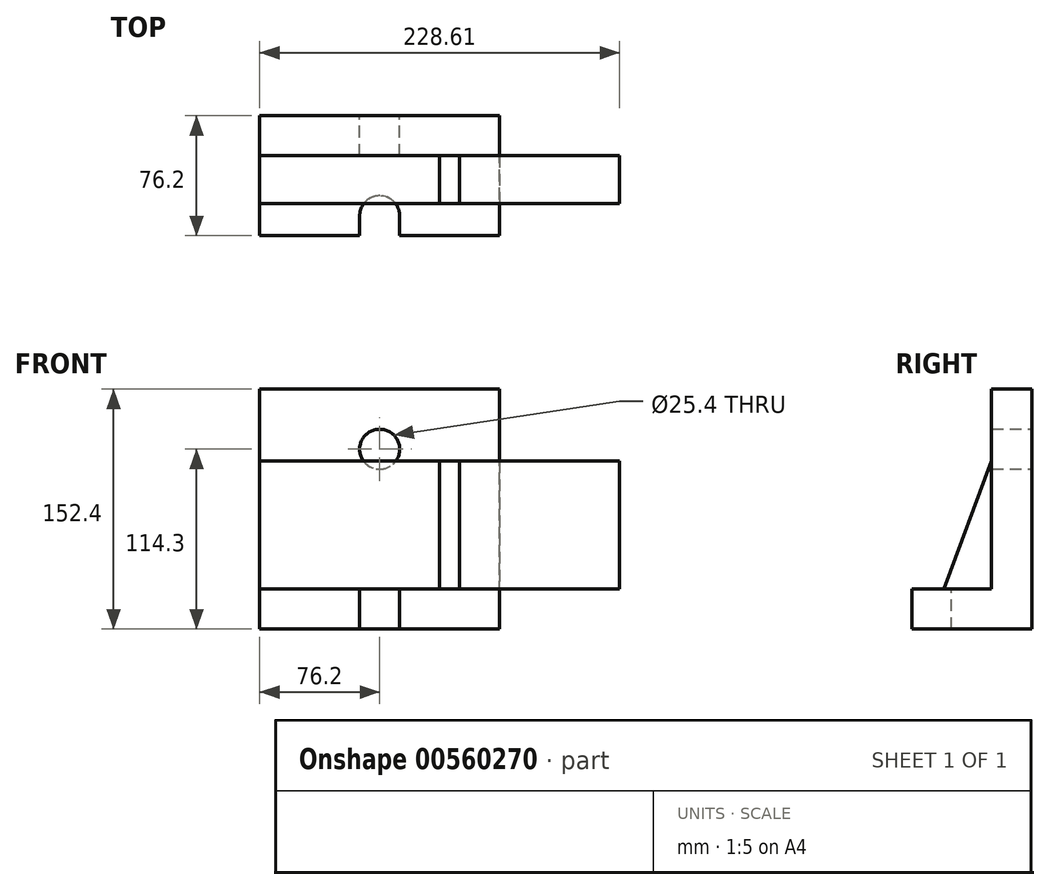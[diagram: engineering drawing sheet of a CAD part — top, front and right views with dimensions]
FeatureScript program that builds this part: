
annotation { "Feature Type Name" : "Feature", "Feature Type Description" : "" }
export const myFeature = defineFeature(function(context is Context, id is Id, definition is map)
    precondition{}
    {
        {
            var Q0;
            Q0=qCreatedBy(makeId("Right.planeOp"),FACE);
            var sketch = newSketch(context, id + "F0", { "sketchPlane" : qUnion([Q0])});
            skLineSegment(sketch, "E0", {"start": v(0, 0) * mm, "end": v(0, 152.4) * mm});
            skLineSegment(sketch, "E1", {"start": v(0, 152.4) * mm, "end": v(-25.4, 152.4) * mm});
            skLineSegment(sketch, "E2", {"start": v(-25.4, 152.4) * mm, "end": v(-25.4, 25.4) * mm});
            skLineSegment(sketch, "E3", {"start": v(-25.4, 25.4) * mm, "end": v(-76.2, 25.4) * mm});
            skLineSegment(sketch, "E4", {"start": v(-76.2, 25.4) * mm, "end": v(-76.2, 0) * mm});
            skLineSegment(sketch, "E5", {"start": v(-76.2, 0) * mm, "end": v(0, 0) * mm});
            skSolve(sketch);
        }
        {
            var Q0;
            Q0=makeQuery(id+"F0.imprint","IMPRINT",FACE,{"disambiguationData":[TD([[makeQuery(id+"F0.imprint","IMPRINT",EDGE,{"derivedFrom":sQuery(id+"F0.wireOp",EDGE,"E0")}),1.0]])]});
            extrude(context, id + "F1", {"entities" : qUnion([Q0]), "endBound" : BoundingType.SYMMETRIC, "depth" : 152.4 * mm, "offsetDistance" : 25.4 * mm});
        }
        {
            var Q0;
            Q0=makeQuery(id+"F1.opExtrude","SWEPT_FACE",FACE,{"disambiguationData":[OSD([sQuery(id+"F0.wireOp",EDGE,"E0")])]});
            var sketch = newSketch(context, id + "F2", { "sketchPlane" : qUnion([Q0])});
            skCircle(sketch, "E6", {"center": v(0, 114.3) * mm, "radius": 12.7 * mm});
            skPoint(sketch, "E6.centerSnap0", {"position": v(0, 152.4) * mm});
            skSolve(sketch);
        }
        {
            var Q0;
            Q0=makeQuery(id+"F2.imprint","IMPRINT",FACE,{"disambiguationData":[TD([[makeQuery(id+"F2.imprint","IMPRINT",EDGE,{"derivedFrom":sQuery(id+"F2.wireOp",EDGE,"E6")}),1.0]])]});
            extrude(context, id + "F3", {"entities" : qUnion([Q0]), "operationType" : NewBodyOperationType.REMOVE, "endBound" : BoundingType.THROUGH_ALL, "oppositeDirection" : true, "depth" : 25.4 * mm, "offsetDistance" : 25.4 * mm});
        }
        {
            var Q0;
            Q0=makeQuery(id+"F1.opExtrude","SWEPT_FACE",FACE,{"disambiguationData":[OSD([sQuery(id+"F0.wireOp",EDGE,"E3")])]});
            var sketch = newSketch(context, id + "F4", { "sketchPlane" : qUnion([Q0])});
            skCircle(sketch, "E7", {"center": v(0, -63.5) * mm, "radius": 12.7 * mm});
            skPoint(sketch, "E7.centerSnap0", {"position": v(0, -76.2) * mm});
            skLineSegment(sketch, "E8", {"start": v(-12.7, -63.5) * mm, "end": v(-12.7, -76.2) * mm});
            skLineSegment(sketch, "E9", {"start": v(12.7, -63.5) * mm, "end": v(12.7, -76.2) * mm});
            skSolve(sketch);
        }
        {
            var Q0;
            {var subQ0=sQuery(id+"F4.wireOp",EDGE,"E7");var subQ1=makeQuery(id+"F4.imprint","INTERSECT",VERTEX,{"derivedFrom":[subQ0,sQuery(id+"F4.wireOp",EDGE,"E8")]});Q0=makeQuery(id+"F4.imprint","IMPRINT",FACE,{"disambiguationData":[TD([[makeQuery(id+"F4.imprint","IMPRINT",EDGE,{"disambiguationData":[TD([[subQ1,1.0]])],"derivedFrom":subQ0}),1.0]])]});}
            var Q1;
            {var subQ0=sQuery(id+"F4.wireOp",EDGE,"E8");Q1=makeQuery(id+"F4.imprint","IMPRINT",FACE,{"disambiguationData":[TD([[makeQuery(id+"F4.imprint","IMPRINT",EDGE,{"derivedFrom":subQ0}),1.0]])]});}
            var Q2;
            {var subQ0=sQuery(id+"F4.wireOp",EDGE,"E9");Q2=makeQuery(id+"F4.imprint","IMPRINT",FACE,{"disambiguationData":[TD([[makeQuery(id+"F4.imprint","IMPRINT",EDGE,{"derivedFrom":subQ0}),-1.0]])]});}
            extrude(context, id + "F5", {"entities" : qUnion([Q0, Q1, Q2]), "operationType" : NewBodyOperationType.REMOVE, "endBound" : BoundingType.THROUGH_ALL, "oppositeDirection" : true, "depth" : 25.4 * mm, "offsetDistance" : 25.4 * mm});
        }
        {
            var Q0;
            Q0=qCreatedBy(makeId("Right.planeOp"),FACE);
            cPlane(context, id + "F6", {"entities" : qUnion([Q0]), "cplaneType" : CPlaneType.OFFSET, "offset" : 50.8 * mm, "width" : 152.4 * mm, "height" : 152.4 * mm});
        }
        {
            var Q0;
            Q0=qCreatedBy(id+"F6.planeOp",FACE);
            var sketch = newSketch(context, id + "F7", { "sketchPlane" : qUnion([Q0])});
            skLineSegment(sketch, "E10.0", {"start": v(-25.4, 106.68) * mm, "end": v(-25.4, 25.4) * mm});
            skLineSegment(sketch, "E10.1", {"start": v(-25.4, 25.4) * mm, "end": v(-55.88, 25.4) * mm});
            skLineSegment(sketch, "E11", {"start": v(-25.4, 106.68) * mm, "end": v(-55.88, 25.4) * mm});
            skSolve(sketch);
        }
        {
            var Q0;
            Q0 = qSketchRegion(id + "F7", true);
            extrude(context, id + "F8", {"entities" : qUnion([Q0]), "operationType" : NewBodyOperationType.ADD, "oppositeDirection" : true, "depth" : 12.7 * mm, "offsetDistance" : 25.4 * mm});
        }
        {
            var Q0;
            Q0=makeQuery(id+"F1.opExtrude","CAP_FACE",FACE,{"disambiguationData":[OSD([sQuery(id+"F0.wireOp",EDGE,"E0"),sQuery(id+"F0.wireOp",EDGE,"E1"),sQuery(id+"F0.wireOp",EDGE,"E2"),sQuery(id+"F0.wireOp",EDGE,"E3"),sQuery(id+"F0.wireOp",EDGE,"E4"),sQuery(id+"F0.wireOp",EDGE,"E5")])],"isStart":true});
            var sketch = newSketch(context, id + "F9", { "sketchPlane" : qUnion([Q0])});
            skLineSegment(sketch, "E12.0", {"start": v(25.4, 106.68) * mm, "end": v(25.4, 25.4) * mm});
            skLineSegment(sketch, "E12.1", {"start": v(25.4, 25.4) * mm, "end": v(55.88, 25.4) * mm});
            skLineSegment(sketch, "E13", {"start": v(25.4, 106.68) * mm, "end": v(55.88, 25.4) * mm});
            skSolve(sketch);
        }
        {
            var Q0;
            Q0=makeQuery(id+"F9.imprint","IMPRINT",FACE,{"disambiguationData":[TD([[makeQuery(id+"F9.imprint","IMPRINT",EDGE,{"derivedFrom":sQuery(id+"F9.wireOp",EDGE,"E12.0")}),1.0]])]});
            extrude(context, id + "F10", {"entities" : qUnion([Q0]), "endBound" : BoundingType.THROUGH_ALL, "oppositeDirection" : true, "depth" : 12.7 * mm, "offsetDistance" : 25.4 * mm});
        }
    });
